# Revit family: QF_ELECTROLUXPROFESSIONAL_1LSNC5_IC64832_E
name_source: partatom
category: Attrezzature speciali
units: mm (PartAtom-declared; Revit-internal decimal feet)

## family parameters
Basato su piano di lavoro = No
Condiviso = No
Punto di calcolo locali = No
Quota connettore circolare = Usa diametro
Sempre verticale = Sì
Taglio con vuoti quando caricato = No
Tipo di parte = Normale

## types (11) — shared parameters
Depth Actual = 1110 mm
Height Actual = 1270 mm  [stored 4.16667 ft]
Latent Heat Output = 0.0
Length Actual = 3835 mm
Modello = IC64832
Phase = 3
Produttore = Electrolux Professional
Sensible Heat Output = 0.0
URL = www.electroluxprofessional.com
Volts = 400 V
Weight = 1040
zero-valued in all types: Gas KW, Prospetto di default, Steam Pounds per Hour

## per-type parameters (varying)
| type | Cycle | Descrizione | Item Number | Watts |
| 9882030124 | 50 Hz | IRONER CYLINDER IC64832 3170MM SUPERIOR EL. CE 400/50/3 DUBIXIUM FR FEED ALONE VAC.FEED.TABLE | 1L0GMR | 56750 W |
| 9882030137 | 50 Hz | IRONER CYLINDER IC64832 3170MM PERFORMANCE EL. CE 400/50/3 DUBIXIUM ML VAC.FEED.TABLE | 1LSPEC | 56750 W |
| 9882030256 | 60 Hz | IRONER CYLINDER IC64832 3170MM ACTIVE EL. CE 400/60/3 6MM SST CYL. EN, ES, PO FEED NOW | 1L82AJ | 56750 W |
| 9882030123 | 50 Hz | IRONER CYLINDER IC64832 3170MM PERFORMANCE EL. CE 400/50/3 DUBIXIUM FR VAC.FEED.TABLE | 1L0GMP | 56750 W |
| 9882030200 | 50 Hz | IRONER CYLINDER IC64832 3170MM ACTIVE EL. CE 400/50/3 6MM SST CYL. FR FEED NOW | 1L826Z | 56750 W |
| 9882030220 | 50 Hz | IRONER CYLINDER IC64832 3170MM EL. CE 400/50/3 DUBIXIUM FR VAC.FEED.TABLE DIAMMS | 1L0GU8 | 56750 W |
| 9882030219 | 50 Hz | IRONER CYLINDER IC64832 3170MM EL. CE 400/50/3 DUBIXIUM ML VAC.FEED.TABLE DIAMMS | 1L0GU7 | 56750 W |
| 9882030203 | 50 Hz | IRONER CYLINDER IC64832 3170MM ACTIVE EL. CE 400/50/3 6MM SST CYL. ML FEED NOW | 1L8272 | 56750 W |
| 9882030138 | 50 Hz | IRONER CYLINDER IC64832 3170MM SUPERIOR EL. CE 400/50/3 DUBIXIUM ML FEED ALONE VAC.FEED.TABLE | 1L0GR1 | 56750 W |
| 9882030244 | 50 Hz | IRONER CYLINDER IC64832 3170MM EL. CE 400/50/3 6MM SST CYL. ML DIAMMS | 1L0GXU | 56750 W |
| 9882030301 | 50 Hz | IRONER CYLINDER IC64832 3170MM EL. CE 400/50/3 DUBIXIUM FR FEED ALONE VAC.FEED.TABLE ANTISTATIC | 1LA26X | 5675000 W |

note: [stored X ft] marks values corroborated as IEEE doubles in the binary element streams (Revit-internal decimal feet)

## geometry (parser evidence)
native form markers: Sweep x10
no freeform markers — native parametric forms only
